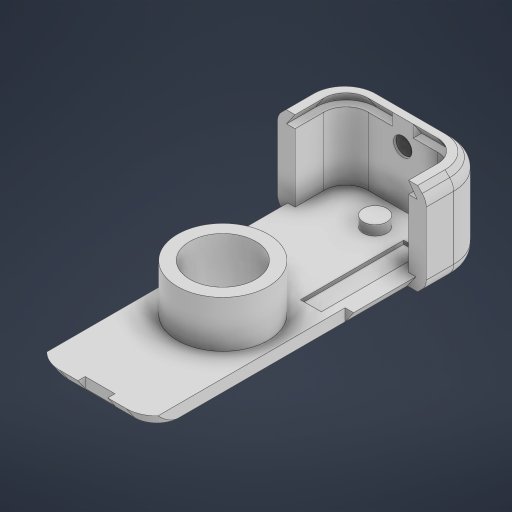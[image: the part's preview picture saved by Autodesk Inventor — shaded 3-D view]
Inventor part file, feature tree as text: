
AUTODESK INVENTOR PART (.ipt)
format: ipt  version: 2023 (Build 270158000, 158)  size: 484,352 bytes
history: native  units: in
note: dims shown in document units (in); Inventor stores cm internally (conversion verified against a paired STEP export)
features: extrude x10, sketch x9, move_body x5, direct_edit x3, sweep x2, chamfer x2, fillet x1
ambient origin geometry x8: Origin, YZ Plane, XZ Plane, XY Plane, X Axis, Y Axis, Z Axis, Center Point
bodies: Solid1 (feature_tree)
feature tree (32):
  extrude  "Extrusion1"  Depth=0.0079in
  extrude  "Extrusion2"  Depth=0.2657in TaperAngle=0.0deg
  direct_edit  "Direct Edit1"
  sketch  "Sketch5"  dims[d1=0.6299in d2=0.0079in]
  sweep  "Sweep1"
  sweep  "Sweep2"
  extrude  "Extrusion13"  Depth=0.0689in
  chamfer  "Chamfer2"  [1 undecoded]
  fillet  "Fillet1"  [1 undecoded]
  direct_edit  "Direct Edit3"
  sketch  "Sketch7"  dims[d13=0.1181in d27=0.5157in]
  extrude  "Extrusion14"  TaperAngle=0.0deg  [1 undecoded]
  direct_edit  "Direct Edit4"
  extrude  "Extrusion18"  Depth=0.0787in
  extrude  "Extrusion15"  TaperAngle=0.0deg  [1 undecoded]
  extrude  "Extrusion16"  TaperAngle=0.0deg  [1 undecoded]
  extrude  "Extrusion17"  TaperAngle=0.0deg  [1 undecoded]
  extrude  "Extrusion19"  Depth=0.0551in
  chamfer  "Chamfer3"  Distance=0.1693in
  extrude  "Extrusion20"  Depth=0.0551in
  sketch  "3D Sketch1"
  sketch  "3D Sketch4"
  sketch  "Sketch6"  dims[d7=0.0689in d8=0.0in d9=0.2657in d10=0.0in]
  sketch  "Sketch8"  dims[d28=0.374in d47=0.0in d48=0.0in d49=0.189in]
  sketch  "Sketch9"  dims[d50=0.3779in d51=0.0689in d52=0.0in d53=0.0in d54=0.0in d55=0.0in]
  sketch  "Sketch10"  dims[d58=0.1693in d59=0.0in d60=0.0in]
  sketch  "Sketch11"  dims[d61=0.0492in d62=0.0787in d63=45.0deg d64=0.0787in d70=0.0in d71=0.0in d72=-0.0059in d73=0.0in d74=0.0in d75=-0.0059in d76=0.0in d77=0.0in d78=-0.0059in d80=0.1398in d81=0.1693in d82=0.1043in d83=0.3937in d84=0.0in d85=0.0787in d86=0.0in d87=0.0in d88=0.0in d89=-0.5709in d90=0.3543in d91=0.0in d92=0.0in d93=0.2087in d94=0.2165in d96=0.8031in d97=0.1181in d98=0.0197in d99=0.0in d100=0.1181in d101=0.0197in d102=0.0in d104=0.5217in d105=0.4291in d107=1.0157in d109=0.1004in d110=0.0925in d111=0.1181in d112=0.2165in d113=0.1181in d114=0.0591in d115=0.0in d116=0.0591in d117=0.0787in d118=45.0deg d119=0.1339in d120=0.0906in d121=0.0551in d122=0.0in d11=0.0197in d12=0.0344in d33=0.0197in d34=0.0344in d35=0.0197in d36=0.0344in d65=0.0197in d66=0.0344in d67=0.0197in d68=0.0344in d103=0.0197in d106=0.0344in]
  move_body  "Move1"
  move_body  "Move3"
  move_body  "Move4"
  move_body  "Move5"
  move_body  "Move6"
note: 6 required parameter values undecoded (feature->parameter linkage not recoverable at this tier; creation-order binding heuristic only, values carry confidence <= 0.55)
